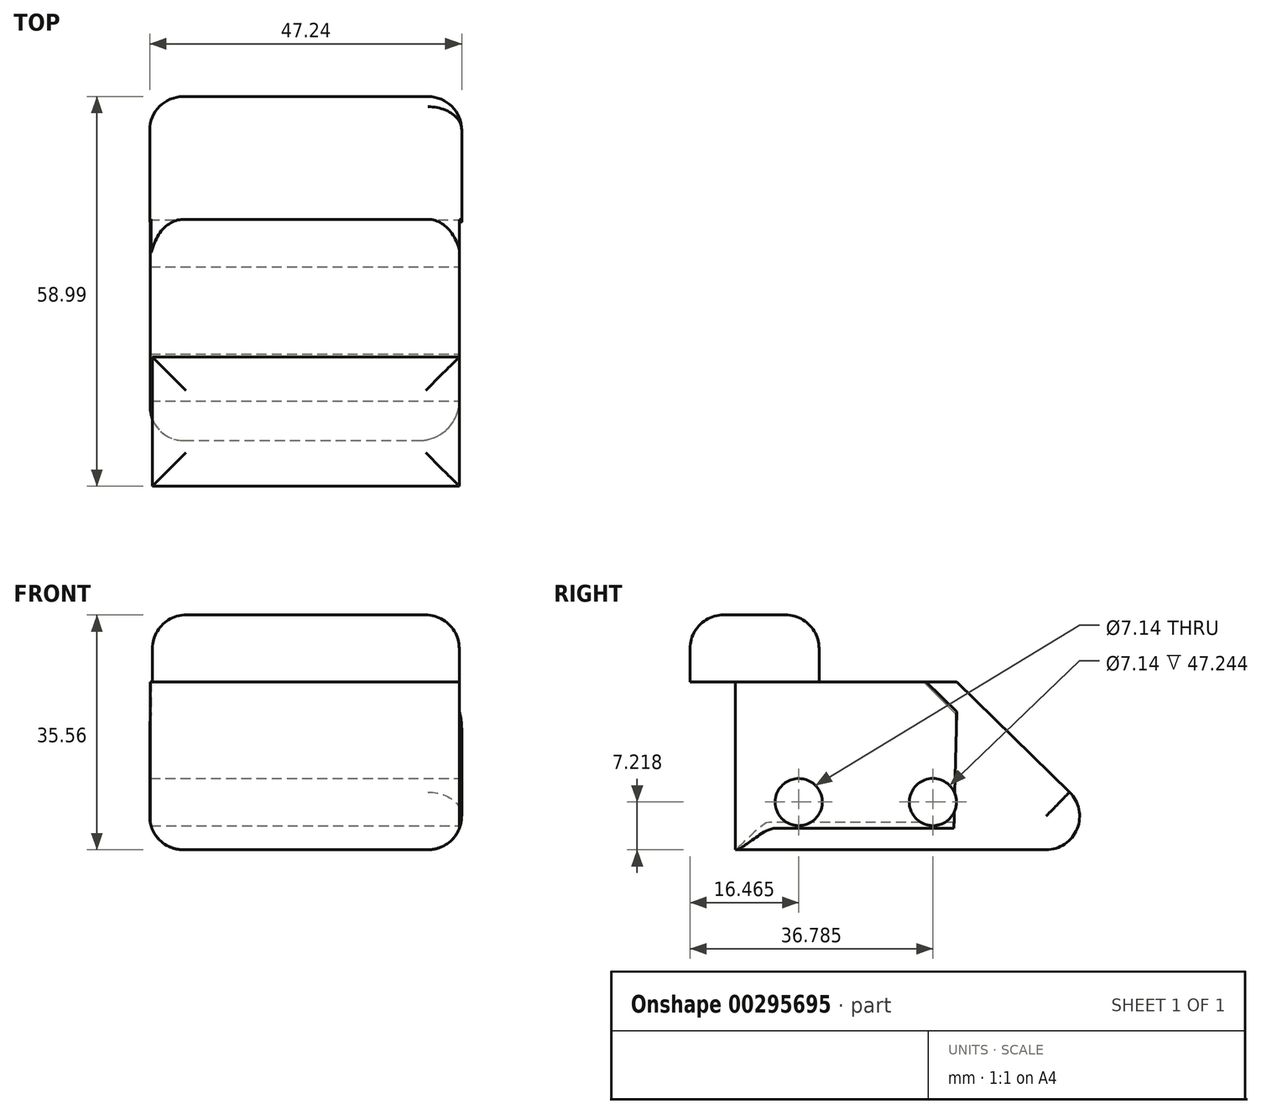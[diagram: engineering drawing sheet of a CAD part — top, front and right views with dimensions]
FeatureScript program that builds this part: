
annotation { "Feature Type Name" : "Feature", "Feature Type Description" : "" }
export const myFeature = defineFeature(function(context is Context, id is Id, definition is map)
    precondition{}
    {
        {
            var Q0;
            Q0=qCreatedBy(makeId("Top.planeOp"),FACE);
            var sketch = newSketch(context, id + "F0", { "sketchPlane" : qUnion([Q0])});
            skLineSegment(sketch, "E0.bottom", {"start": v(-23.02, 20.91) * mm, "end": v(23.8, 20.91) * mm});
            skLineSegment(sketch, "E0.top", {"start": v(-23.02, -12.66) * mm, "end": v(23.8, -12.66) * mm});
            skLineSegment(sketch, "E0.left", {"start": v(-23.02, 20.91) * mm, "end": v(-23.02, -12.66) * mm});
            skLineSegment(sketch, "E0.right", {"start": v(23.8, 20.91) * mm, "end": v(23.8, -12.66) * mm});
            skSolve(sketch);
        }
        {
            var Q0;
            Q0 = qSketchRegion(id + "F0", true);
            extrude(context, id + "F1", {"entities" : qUnion([Q0]), "depth" : 25.4 * mm});
        }
        {
            var Q0;
            Q0=qCreatedBy(makeId("Right.planeOp"),FACE);
            var sketch = newSketch(context, id + "F2", { "sketchPlane" : qUnion([Q0])});
            skPoint(sketch, "E1.start.orphan", {"position": v(46.82, 0) * mm});
            skLineSegment(sketch, "E2", {"start": v(20.91, 25.33) * mm, "end": v(46.82, 0) * mm});
            skLineSegment(sketch, "E3", {"start": v(46.82, 0) * mm, "end": v(20.34, 0) * mm});
            skLineSegment(sketch, "E4", {"start": v(20.34, 0) * mm, "end": v(20.91, 25.33) * mm});
            skSolve(sketch);
        }
        {
            var Q0;
            Q0 = qSketchRegion(id + "F2", true);
            extrude(context, id + "F3", {"entities" : qUnion([Q0]), "operationType" : NewBodyOperationType.ADD, "depth" : 24.13 * mm, "hasSecondDirection" : true, "secondDirectionOppositeDirection" : true, "secondDirectionDepth" : 23.1 * mm});
        }
        {
            var Q0;
            Q0=qCreatedBy(makeId("Right.planeOp"),FACE);
            var sketch = newSketch(context, id + "F4", { "sketchPlane" : qUnion([Q0])});
            skLineSegment(sketch, "E5", {"start": v(38.76, 7.87) * mm, "end": v(38.76, 0) * mm});
            skSolve(sketch);
        }
        {
            var Q0;
            Q0=qCreatedBy(makeId("Front.planeOp"),FACE);
            var sketch = newSketch(context, id + "F5", { "sketchPlane" : qUnion([Q0])});
            skLineSegment(sketch, "E6.bottom", {"start": v(-22.7, 25.43) * mm, "end": v(23.76, 25.43) * mm});
            skLineSegment(sketch, "E6.top", {"start": v(-22.7, 35.56) * mm, "end": v(23.76, 35.56) * mm});
            skLineSegment(sketch, "E6.left", {"start": v(-22.7, 25.43) * mm, "end": v(-22.7, 35.56) * mm});
            skLineSegment(sketch, "E6.right", {"start": v(23.76, 25.43) * mm, "end": v(23.76, 35.56) * mm});
            skSolve(sketch);
        }
        {
            var Q0;
            Q0 = qSketchRegion(id + "F5", true);
            extrude(context, id + "F6", {"entities" : qUnion([Q0]), "depth" : 19.56 * mm});
        }
        {
            var Q0;
            Q0=makeQuery(id+"F1.opExtrude","SWEPT_EDGE",EDGE,{"disambiguationData":[OSD([sQuery(id+"F0.wireOp",EDGE,"E0.top"),sQuery(id+"F0.wireOp",EDGE,"E0.right")])]});
            fillet(context, id + "F7", {"entities" : qUnion([Q0]), "radius" : 6.13 * mm, "tangentPropagation" : true, "allowEdgeOverflow" : false});
        }
        {
            var Q0;
            Q0=makeQuery(id+"F1.opExtrude","SWEPT_EDGE",EDGE,{"disambiguationData":[OSD([sQuery(id+"F0.wireOp",EDGE,"E0.top"),sQuery(id+"F0.wireOp",EDGE,"E0.left")])]});
            fillet(context, id + "F8", {"entities" : qUnion([Q0]), "radius" : 5.08 * mm, "tangentPropagation" : true, "allowEdgeOverflow" : false});
        }
        {
            var Q0;
            Q0=makeQuery(id+"F3.opExtrude","CAP_EDGE",EDGE,{"disambiguationData":[OSD([sQuery(id+"F2.wireOp",EDGE,"E2")])],"isStart":false});
            var Q1;
            Q1=makeQuery(id+"F3.opExtrude","SWEPT_EDGE",EDGE,{"disambiguationData":[OSD([sQuery(id+"F2.wireOp",EDGE,"E2"),sQuery(id+"F2.wireOp",EDGE,"E3")])]});
            fillet(context, id + "F9", {"entities" : qUnion([Q0, Q1]), "radius" : 5.08 * mm, "tangentPropagation" : true, "allowEdgeOverflow" : false});
        }
        {
            var Q0;
            Q0=makeQuery(id+"F6.opExtrude","SWEPT_EDGE",EDGE,{"disambiguationData":[OSD([sQuery(id+"F5.wireOp",EDGE,"E6.top"),sQuery(id+"F5.wireOp",EDGE,"E6.right")])]});
            var Q1;
            Q1=makeQuery(id+"F6.opExtrude","SWEPT_EDGE",EDGE,{"disambiguationData":[OSD([sQuery(id+"F5.wireOp",EDGE,"E6.top"),sQuery(id+"F5.wireOp",EDGE,"E6.left")])]});
            var Q2;
            Q2=makeQuery(id+"F6.opExtrude","CAP_EDGE",EDGE,{"disambiguationData":[OSD([sQuery(id+"F5.wireOp",EDGE,"E6.top")])],"isStart":false});
            var Q3;
            Q3=makeQuery(id+"F6.opExtrude","CAP_EDGE",EDGE,{"disambiguationData":[OSD([sQuery(id+"F5.wireOp",EDGE,"E6.top")])],"isStart":true});
            fillet(context, id + "F10", {"entities" : qUnion([Q0, Q1, Q2, Q3]), "radius" : 5.08 * mm, "tangentPropagation" : true, "allowEdgeOverflow" : false});
        }
        {
            var Q0;
            Q0=makeQuery(id+"F3.opExtrude","CAP_EDGE",EDGE,{"disambiguationData":[OSD([sQuery(id+"F2.wireOp",EDGE,"E2")])],"isStart":true});
            fillet(context, id + "F11", {"entities" : qUnion([Q0]), "radius" : 5.08 * mm, "tangentPropagation" : true, "allowEdgeOverflow" : false});
        }
        {
            var Q0;
            Q0=makeQuery(id+"F1.opExtrude","CAP_EDGE",EDGE,{"disambiguationData":[OSD([sQuery(id+"F0.wireOp",EDGE,"E0.bottom")])],"isStart":false});
            chamfer(context, id + "F12", {"entities" : qUnion([Q0]), "width" : 5.08 * mm, "tangentPropagation" : true});
        }
        {
            var Q0;
            Q0=makeQuery(id+"F3.opExtrude","CAP_EDGE",EDGE,{"disambiguationData":[OSD([sQuery(id+"F2.wireOp",EDGE,"E3")])],"isStart":false});
            fillet(context, id + "F13", {"entities" : qUnion([Q0]), "radius" : 5.08 * mm, "tangentPropagation" : true, "allowEdgeOverflow" : false});
        }
        {
            var Q0;
            Q0=qCreatedBy(makeId("Right.planeOp"),FACE);
            var sketch = newSketch(context, id + "F14", { "sketchPlane" : qUnion([Q0])});
            skCircle(sketch, "E7", {"center": v(17.22, 7.22) * mm, "radius": 3.57 * mm});
            skCircle(sketch, "E8", {"center": v(-3.1, 7.22) * mm, "radius": 3.57 * mm});
            skSolve(sketch);
        }
        {
            var Q0;
            Q0 = qSketchRegion(id + "F14", true);
            extrude(context, id + "F15", {"entities" : qUnion([Q0]), "operationType" : NewBodyOperationType.REMOVE, "endBound" : BoundingType.THROUGH_ALL, "oppositeDirection" : true, "depth" : 25.4 * mm, "hasSecondDirection" : true, "secondDirectionBound" : SecondDirectionBoundingType.THROUGH_ALL, "secondDirectionOppositeDirection" : false, "secondDirectionDepth" : 30.99 * mm});
        }
    });
